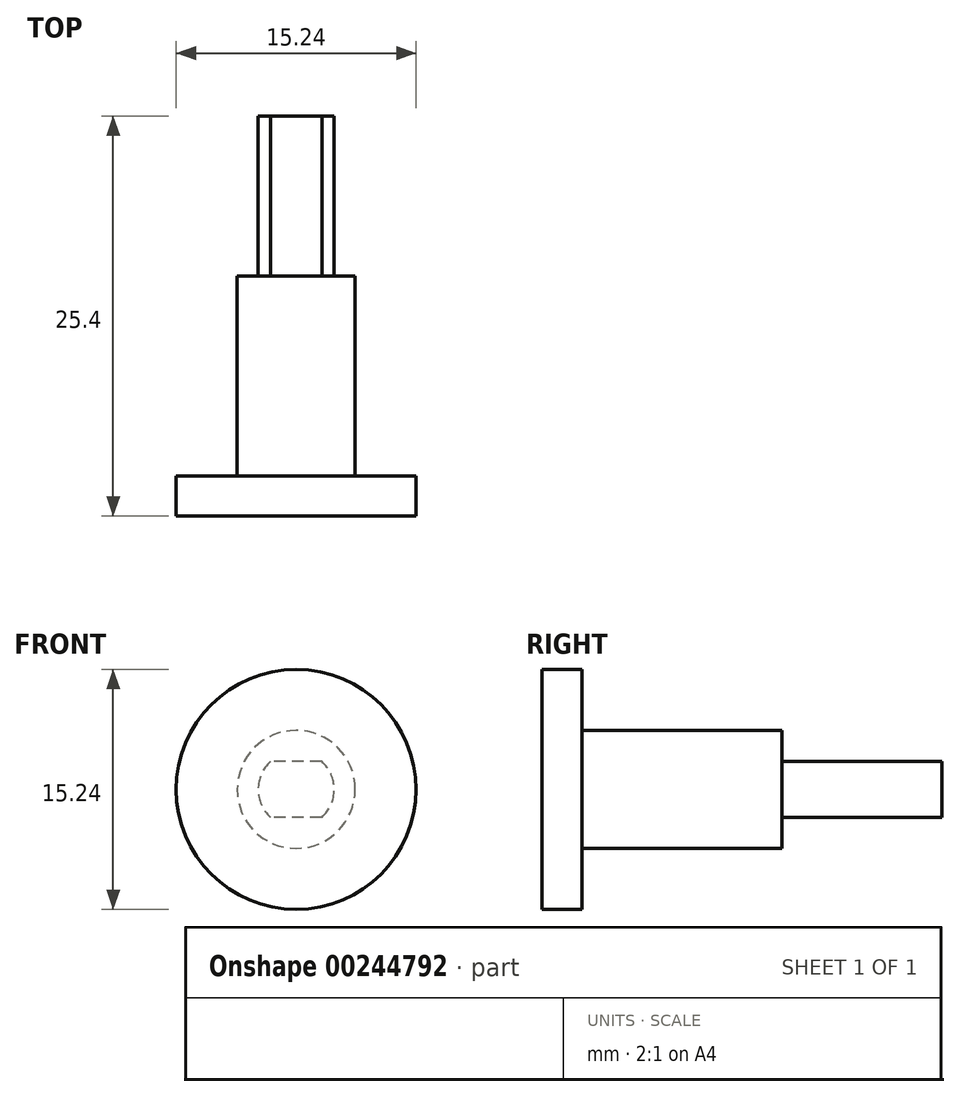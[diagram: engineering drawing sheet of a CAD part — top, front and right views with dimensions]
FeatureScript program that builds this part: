
annotation { "Feature Type Name" : "Feature", "Feature Type Description" : "" }
export const myFeature = defineFeature(function(context is Context, id is Id, definition is map)
    precondition{}
    {
        {
            var Q0;
            Q0=qCreatedBy(makeId("Front.planeOp"),FACE);
            var sketch = newSketch(context, id + "F0", { "sketchPlane" : qUnion([Q0])});
            skLineSegment(sketch, "E0", {"start": v(0, 0) * mm, "end": v(0, 1.78) * mm});
            skLineSegment(sketch, "E1", {"start": v(0, 0) * mm, "end": v(0, -1.78) * mm});
            skLineSegment(sketch, "E2", {"start": v(0, 0) * mm, "end": v(-2.41, 0) * mm});
            skLineSegment(sketch, "E3", {"start": v(0, 0) * mm, "end": v(2.41, 0) * mm});
            skArc(sketch, "E4", {"start": v(-1.63, 1.78) * mm, "mid": v(-2.41, 0) * mm, "end": v(-1.63, -1.78) * mm});
            skLineSegment(sketch, "E5", {"start": v(0, 1.78) * mm, "end": v(-1.63, 1.78) * mm});
            skLineSegment(sketch, "E6", {"start": v(0, 1.78) * mm, "end": v(1.63, 1.78) * mm});
            skLineSegment(sketch, "E7", {"start": v(0, -1.78) * mm, "end": v(-1.63, -1.78) * mm});
            skLineSegment(sketch, "E8", {"start": v(0, -1.78) * mm, "end": v(1.63, -1.78) * mm});
            skArc(sketch, "E9.trimOffspring", {"start": v(1.63, -1.78) * mm, "mid": v(2.41, 0) * mm, "end": v(1.63, 1.78) * mm});
            skSolve(sketch);
        }
        {
            var Q0;
            Q0 = qSketchRegion(id + "F0", true);
            extrude(context, id + "F1", {"entities" : qUnion([Q0]), "depth" : 10.16 * mm});
        }
        {
            var Q0;
            Q0=makeQuery(id+"F1.opExtrude","CAP_FACE",FACE,{"disambiguationData":[OSD([sQuery(id+"F0.wireOp",EDGE,"E4"),sQuery(id+"F0.wireOp",EDGE,"E5"),sQuery(id+"F0.wireOp",EDGE,"E6"),sQuery(id+"F0.wireOp",EDGE,"E7"),sQuery(id+"F0.wireOp",EDGE,"E8"),sQuery(id+"F0.wireOp",EDGE,"E9.trimOffspring")])],"isStart":false});
            var sketch = newSketch(context, id + "F2", { "sketchPlane" : qUnion([Q0])});
            skCircle(sketch, "E10", {"center": v(0, 0) * mm, "radius": 3.75 * mm});
            skSolve(sketch);
        }
        {
            var Q0;
            Q0 = qSketchRegion(id + "F2", true);
            extrude(context, id + "F3", {"entities" : qUnion([Q0]), "operationType" : NewBodyOperationType.ADD, "depth" : 12.7 * mm});
        }
        {
            var Q0;
            Q0=makeQuery(id+"F3.opExtrude","CAP_FACE",FACE,{"disambiguationData":[OSD([sQuery(id+"F2.wireOp",EDGE,"E10")])],"isStart":false});
            var sketch = newSketch(context, id + "F4", { "sketchPlane" : qUnion([Q0])});
            skCircle(sketch, "E11", {"center": v(0, 0) * mm, "radius": 7.62 * mm});
            skSolve(sketch);
        }
        {
            var Q0;
            Q0 = qSketchRegion(id + "F4", true);
            extrude(context, id + "F5", {"entities" : qUnion([Q0]), "operationType" : NewBodyOperationType.ADD, "depth" : 2.54 * mm});
        }
    });
